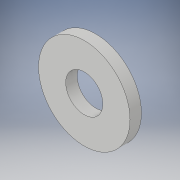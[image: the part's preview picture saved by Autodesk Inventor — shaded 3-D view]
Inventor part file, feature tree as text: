
AUTODESK INVENTOR PART (.ipt)
format: ipt  version: 2018 (Build 220112000, 112)  size: 97,280 bytes
history: native  units: in
note: dims shown in document units (in); Inventor stores cm internally (conversion verified against a paired STEP export)
features: extrude x1, sketch x1
ambient origin geometry x8: Origin, YZ Plane, XZ Plane, XY Plane, X Axis, Y Axis, Z Axis, Center Point
bodies: Solid1 (feature_tree)
feature tree (2):
  extrude  "Extrusion1"  Depth=0.0625in
  sketch  "Sketch1"  dims[d0=0.5in d1=0.2031in d2=0.0625in d3=0.0in]
